# Revit family: BC_Aircalo_BORA-120-STD-Gauche_LOD200_
name_source: partatom
category: Equipement de génie climatique
revit_build: Autodesk Revit 2017 (Build: 20160225_1515(x64)
units: mm (PartAtom-declared; Revit-internal decimal feet)

## family parameters
Basée sur le plan de construction = Non
Cote de connecteur circulaire = Utiliser le diamètre
Couper avec des vides une fois chargée = Non
Numéro OmniClass = 23.75.70.17.27
Partagée = Non
Point de calcul de pièce = Non
Titre OmniClass = Fan Coil Units
Toujours verticalement = Non
Type d'élément = Normal

## types (2) — shared parameters
Connection Diameter = 19.05 mm
Fabricant = Aircalo
Filter class = G3;G4
Insulation Material = Mousse polyuréthane ignifugé 20mm
Length Cassette = 1196.00 mm
Main Material = Acier galvanisé
Manufacturer Product Link = http://aircalo.fr
Mass = 30.00 kg
Modèle = Bora Standard
Motor power absorbed = 100 W
New Air Diameter = 125.00 mm
Nominal Voltage = 230 V
Outlet Diameter = 16.00 mm
Overall Length = 1466.00 mm
Overall Width = 599.00 mm
Product Code = B3A
Second Diameter = 12.70 mm
Thin line THK = 0.00 mm

## per-type parameters (varying)
| type | Overall Height |
| Bora 60 Standard - Hauteur 300mm | 300.00 mm |
| Bora 60 Standard - Hauteur 380mm | 380.00 mm |

## geometry (parser evidence)
native form markers: Sweep x8
no freeform markers — native parametric forms only
